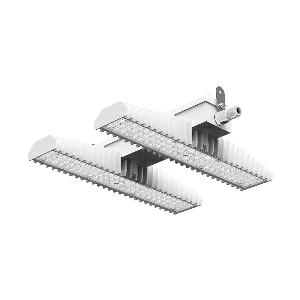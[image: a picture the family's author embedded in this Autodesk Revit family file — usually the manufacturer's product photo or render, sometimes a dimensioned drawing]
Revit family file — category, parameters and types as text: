
# Revit family: 3f_filippi_-_3f_lem_ampio_3f_filippi_-_58882_-_3f_lem_2_led_100_cr_ampio
name_source: partatom
category: Lighting Fixtures
units: mm (PartAtom-declared; Revit-internal decimal feet)

## family parameters
Cut with Voids When Loaded = No
Host = Face
Light Source = No
Part Type = Normal
Room Calculation Point = No
Round Connector Dimension = Use Diameter
Shared = No

## types (1)
- 3F Filippi - 3F LEM Ampio (1 x LED, 16989 lm, 109 W, 4000 K)
    Apparent Load = 109 VA
    Approval mark = CE
    CIE Flux Codes = 60 92 99 100 100
    Color Rendering = 80
    Color Temperature = 4000 K
    Control Gear = Electronic ballast
    Default Elevation = 1800 mm
    Description = Industrial luminaire with high light output and high luminous efficiency designed with the most innovative technologies for environments with temperature up to 55°C.

ILLUMINOTECHNICAL
Luminous efficiency 100% (DLOR 100%, ULOR 0%).
Initial luminous flux of the luminaire 16989 lm.
Direct symmetric wide distribution: the illuminated area has a rectangular shape.
Installation Interdistance Transv.D = 1.58 x hu - Long.D = 1.45 x hu.
Tabular UGR (CIE 117 - 4H-8H; S=0.25H; 70/50/20): RUG 22.5 - 23.5.
Beam angle: 93° - 99°.
Luminous efficacy 156 lm/W.
Lifetime (L93/B10): 30000 h. (tq+25°C)
Lifetime (L90/B10): 50000 h. (tq+25°C)
Lifetime (L85/B10): 80000 h. (tq+25°C)
Lifetime (L80/B10): 100000 h. (tq+25°C)
Lifetime (L85/B10): 50000 h. (tq+55°C)
Sudden decreased luminous flux after 50000 hours: 0% (C0).
Photobiological safety in compliance with IEC/TR 62778: RG0 risk exempt, (IEC 62471).
In compliance with IEC/EN 62722-2-1 - IEC/EN 62717 standards.

SOURCE
2 Mid-Power linear LED modules 50W/840.
Energy efficiency class (UE 2019/2020 - UE 2019/2015): C.
CIE 13.3 Colour rendering index: CRI >80 (R9 <50%).
IES TM-30 Fidelity Index: Rf = 84 Rg = 95.
CCT nominal colour temperature 4000 K.
Colour initial tolerance (MacAdam): SDCM 3.

MECHANICAL
Passive modular heatsinks in die-casted aluminium, painted in white colour.
To optimize the thermal management of the LED module, the heatsinks are oversized and provided with self-cleaning of cooling fins.
Wiring body in aluminium and galvanised steel anchored solidly to the sinks and thermally separated.
3F Lens lenses with high luminous efficiency, transparent methacrylate (PMMA), fixed to the LED modules.
Fixing brackets in stainless steel.
Luminaire with limited surface temperature. - D - (EN 60598-2-24)
Dimensions: 470x542 mm, height 129 mm. Weight 9.125 kg.
IP65 protection degree.
Mechanical strength to impacts IK06 (1 joule).
Glow-wire test resistance 650°C.

ELECTRICAL
Halogen Free electronic wiring 230V-50/60Hz, power factor 0.97, THD <25%, constant output current, class I, 1 driver.
Power of the luminaire 109 W.
ENEC - CE.
SAFE FLICKER: PstLM=<1 and SVM=<0.4 (IEC TR 61547-1 and IEC TR 63158), to ensure a more comfortable and safe light.
Luminaire compliant with EN 60598-2-22 for power supply from a centralised emergency system CPSS (Central Power Supply System), not incorporated in the luminaire - high risk areas excluded. The default power and flux are 100% in AC and 100% in DC.
Ambient temperature from -30°C to +55°C.
Temperature class T6 max 85°C.
Quick connection via M20 3P connector with 9-13 mm tightening range.
Power unit positioned on a separate compartment by the LED module to ensure optimum temperatures of cabling components, to be inspectable and maintainable.
Relative humidity UR: <85%.

INSTALLATION
Ceiling / Suspended / Wall.
All accessories dedicated to this product are available on the Catalog and on our website www.3F-Filippi.com.

APPLICATIONS
In commercial environments, exhibition and industrial areas, stores, open areas.
Applications with high ambient temperature up to 55°C.
Environments in which it is necessary a total protection against falling fragments (eg environments with foodstuffs or machines with moving parts or with extreme temperature changes), use luminaires with polycarbonate lenses.

WARNING
Fixture not suitable for cold stores with an ambient temperature <0°C and/or relative humidity >85%.
Luminaire designed for disposal/recycling at end-of-life.
Replaceable (LED only) light source by a professional. Replaceable control gear by a professional.
    Height = 129 mm
    Lamp = 1 x LED
    Lamp Light Flux = 16989 lm
    Lamp Power = 109 W
    Lamp count = 1
    Length = 470 mm
    Lifetime = 50000 h
    Luminous efficacy = 156 lm/W
    Manufacturer = 3F Filippi
    ModVariant = No
    Model = 3F Filippi - 58882 - 3F LEM 2 LED 100 CR AMPIO
    Mounting Place = Ceiling
    Mounting Type = Pendant
    Number of Poles = 1
    OnlyDefault = Yes
    Power Factor = 1
    Product Name = 3F Filippi - 3F LEM Ampio
    Product group = pendant luminaire
    ProductGroupID = 9
    Protection Class = Protection class I
    Protection Degree = IP 65
    RLX_Detail_Level = 1
    RLX_Emergency_Light_Flux = 0 lm
    RLX_Emergency_Type = 0
    RLX_Emergency_Type_DB = No
    RlxData = <blob elided: 96277 chars, md5=bea0dfdf>
    Socket = socket
    Standby Power = 0 W
    System Light Flux = 16989 lm
    System Power = 109 W
    Type Comments = Product without accessories
    Type Image = 3f_filippi_-_lem_2.jpg
    URL = http://relux.com
    VarID = ---
    Voltage = 0 V
    Weight = 0.00 kg
    Width = 542 mm

## geometry (parser evidence)
native form markers: Blend x4, Sweep x13
no freeform markers — native parametric forms only
